# Revit family: Blucher_PipeFitting_(854-500)aa
name_source: partatom
category: Pipe Fittings
revit_build: Autodesk Revit 2017 (Build: 20190508_0315(x64)
units: mm (PartAtom-declared; Revit-internal decimal feet)

## family parameters
Always vertical = Yes
Cut with Voids When Loaded = No
OmniClass Number = 23.60.30.11.14
OmniClass Title = Pipework Fittings
Part Type = Union
Round Connector Dimension = Use Radius
Shared = No
Work Plane-Based = No

## types (5) — shared parameters
Assembly Code = D20
AssetType = Fixed
BIMObjectName = Blucher_PipeFitting_(854-500)
ClassificationName = Uniclass2015
ClassificationValue = Pr_65_52_63_81
Color = Stainless steel
Description = 843 Range - Stainless steel: AISI304/EN1.4301
DocumentationCertificates = http://www.blucher.com
DocumentationInstallationGuide = http://www.blucher.com
DocumentationLiterature = http://www.blucher.com
DocumentationMaintenance = http://www.blucher.com
DocumentationTechnical = http://www.blucher.com
DurationUnit = Years
ExpectedLife = 50
Finish = Stainless steel
IfcExportAs = IfcPipeFittingType
IfcExportType = IfcPipeFitting
Keynote = S10/110
Loss Method = Not Defined
Manufacturer = Blücher
ManufacturerName = Blücher
Material = Stainless steel
MaterialBlucher = Blucher_Stainless Steel
NBSDescription = Stainless steel waste water pipes and fittings
NBSObjectName = Blucher - Stainless steel waste water pipes and fittings
NBSReference = 90-10-20/350
ProductInstallationVideo = http://www.blucher.com
ProductionYear = 2020
Shape = Cylinder
StainlessSteel304 = Yes
StainlessSteel316 = No
Type Comments = 843 Range - Stainless steel: AISI304/EN1.4301
TypeName = 843 Range - Stainless steel: AISI304/EN1.4301
URL = http://www.blucher.com
WarrantyDurationLabor = 0
WarrantyDurationParts = 0
WarrantyDurationUnit = Years
Weight = 0.00 kg
_BSBibleVersion = 16
_CurrentRevision = 1
_DistributedBy = www.bimstore.co.uk
zero-valued in all types: _BimSpecGuid

## per-type parameters (varying)
| type | ConnectionSize | D | DN110 | DN125 | DN160 | DN50 | DN75 | FD | H1 | NominalDepth | NominalHeight | NominalLength | X5 |
| 854.500.050 | 25 mm  [stored 0.082021 ft] | 50 mm  [stored 0.164042 ft] | No | No | No | Yes | No | 9 mm  [stored 0.0295276 ft] | 12 mm  [stored 0.0393701 ft] | 160 mm  [stored 0.524934 ft] | 64 mm | 160 mm  [stored 0.524934 ft] | 42 mm  [stored 0.137795 ft] |
| 854.500.075 | 38 mm | 75 mm | No | No | No | No | Yes | 11 mm  [stored 0.0360892 ft] | 5 mm  [stored 0.0164042 ft] | 200 mm  [stored 0.656168 ft] | 67 mm | 200 mm  [stored 0.656168 ft] | 50 mm  [stored 0.164042 ft] |
| 854.500.110 | 55 mm  [stored 0.180446 ft] | 110 mm  [stored 0.360892 ft] | Yes | No | No | No | No | 11 mm  [stored 0.0360892 ft] | 4 mm  [stored 0.0131234 ft] | 230 mm  [stored 0.754593 ft] | 73 mm | 230 mm  [stored 0.754593 ft] | 57 mm  [stored 0.187008 ft] |
| 854.500.125 | 63 mm | 125 mm  [stored 0.410105 ft] | No | Yes | No | No | No | 14 mm  [stored 0.0459318 ft] | 5 mm  [stored 0.0164042 ft] | 255 mm  [stored 0.836614 ft] | 80 mm  [stored 0.262467 ft] | 255 mm  [stored 0.836614 ft] | 60 mm  [stored 0.19685 ft] |
| 854.500.160 | 80 mm  [stored 0.262467 ft] | 160 mm  [stored 0.524934 ft] | No | No | Yes | No | No | 14 mm  [stored 0.0459318 ft] | 10 mm  [stored 0.0328084 ft] | 285 mm  [stored 0.935039 ft] | 97 mm | 285 mm  [stored 0.935039 ft] | 72 mm  [stored 0.23622 ft] |

note: column(s) folded — value = type name in every type: Model, ModelReference

note: [stored X ft] marks values corroborated as IEEE doubles in the binary element streams (Revit-internal decimal feet)

## geometry (parser evidence)
native form markers: Blend x2, Sweep x3
no freeform markers — native parametric forms only
